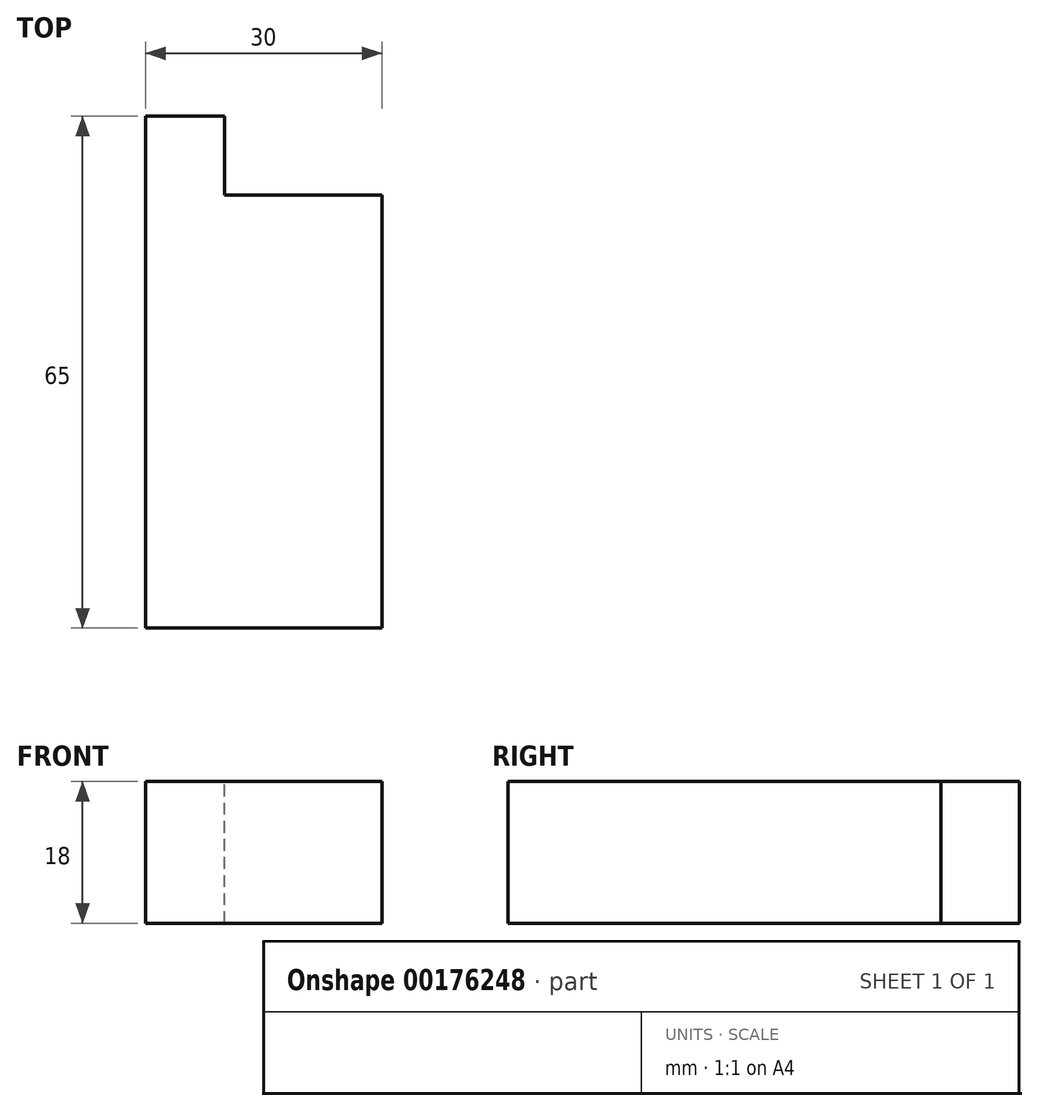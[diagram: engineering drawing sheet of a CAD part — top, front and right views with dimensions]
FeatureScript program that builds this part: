
annotation { "Feature Type Name" : "Feature", "Feature Type Description" : "" }
export const myFeature = defineFeature(function(context is Context, id is Id, definition is map)
    precondition{}
    {
        {
            var Q0;
            Q0=qCreatedBy(makeId("Top.planeOp"),FACE);
            var sketch = newSketch(context, id + "F0", { "sketchPlane" : qUnion([Q0])});
            skLineSegment(sketch, "E0.bottom", {"start": v(-15, 27.5) * mm, "end": v(15, 27.5) * mm});
            skLineSegment(sketch, "E0.top", {"start": v(-15, -27.5) * mm, "end": v(15, -27.5) * mm});
            skLineSegment(sketch, "E0.left", {"start": v(-15, 27.5) * mm, "end": v(-15, -27.5) * mm});
            skLineSegment(sketch, "E0.right", {"start": v(15, 27.5) * mm, "end": v(15, -27.5) * mm});
            skPoint(sketch, "E0.middle", {"position": v(0, 0) * mm});
            skSolve(sketch);
        }
        {
            var Q0;
            Q0=qSketchRegion(id+"F0",true);
            extrude(context, id + "F1", {"entities" : qUnion([Q0]), "depth" : 18 * mm});
        }
        {
            var Q0;
            Q0=makeQuery(id+"F1.opExtrude","SWEPT_FACE",FACE,{"disambiguationData":[OSD([sQuery(id+"F0.wireOp",EDGE,"E0.bottom")])]});
            var sketch = newSketch(context, id + "F2", { "sketchPlane" : qUnion([Q0])});
            skLineSegment(sketch, "E1.bottom", {"start": v(15, 0) * mm, "end": v(5, 0) * mm});
            skLineSegment(sketch, "E1.top", {"start": v(15, 18) * mm, "end": v(5, 18) * mm});
            skLineSegment(sketch, "E1.left", {"start": v(15, 0) * mm, "end": v(15, 18) * mm});
            skLineSegment(sketch, "E1.right", {"start": v(5, 0) * mm, "end": v(5, 18) * mm});
            skSolve(sketch);
        }
        {
            var Q0;
            Q0=qSketchRegion(id+"F2",true);
            extrude(context, id + "F3", {"entities" : qUnion([Q0]), "operationType" : NewBodyOperationType.ADD, "depth" : 10 * mm});
        }
    });
